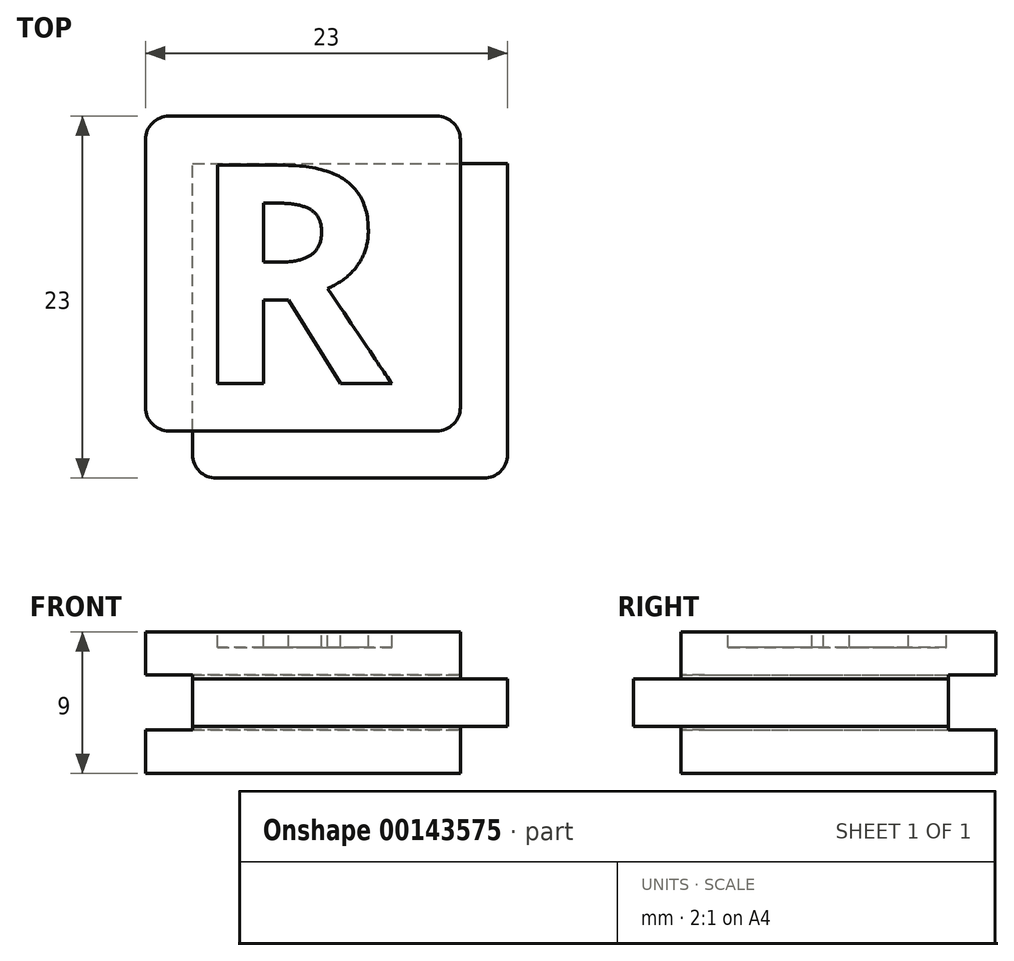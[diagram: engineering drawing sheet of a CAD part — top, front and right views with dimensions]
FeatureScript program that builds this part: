
annotation { "Feature Type Name" : "Feature", "Feature Type Description" : "" }
export const myFeature = defineFeature(function(context is Context, id is Id, definition is map)
    precondition{}
    {
        {
            var Q0;
            Q0=qCreatedBy(makeId("Front.planeOp"),FACE);
            var sketch = newSketch(context, id + "F0", { "sketchPlane" : qUnion([Q0])});
            skLineSegment(sketch, "E0.bottom", {"start": v(10, 4.5) * mm, "end": v(-10, 4.5) * mm});
            skLineSegment(sketch, "E0.top", {"start": v(10, -4.5) * mm, "end": v(-10, -4.5) * mm});
            skLineSegment(sketch, "E0.left", {"start": v(10, 4.5) * mm, "end": v(10, -4.5) * mm});
            skLineSegment(sketch, "E0.right", {"start": v(-10, 4.5) * mm, "end": v(-10, -4.5) * mm});
            skPoint(sketch, "E0.middle", {"position": v(0, 0) * mm});
            skLineSegment(sketch, "E1.bottom", {"start": v(13, 1.5) * mm, "end": v(7, 1.5) * mm});
            skLineSegment(sketch, "E1.top", {"start": v(13, -1.5) * mm, "end": v(7, -1.5) * mm});
            skLineSegment(sketch, "E1.left", {"start": v(13, 1.5) * mm, "end": v(13, -1.5) * mm});
            skLineSegment(sketch, "E1.right", {"start": v(7, 1.5) * mm, "end": v(7, -1.5) * mm});
            skPoint(sketch, "E1.middle", {"position": v(10, 0) * mm});
            skLineSegment(sketch, "E2.bottom", {"start": v(7, 1.5) * mm, "end": v(-7, 1.5) * mm});
            skLineSegment(sketch, "E2.top", {"start": v(7, -1.5) * mm, "end": v(-7, -1.5) * mm});
            skLineSegment(sketch, "E2.right", {"start": v(-7, 1.5) * mm, "end": v(-7, -1.5) * mm});
            skLineSegment(sketch, "E3.bottom", {"start": v(-7, -1.5) * mm, "end": v(-10, -1.5) * mm});
            skLineSegment(sketch, "E3.top", {"start": v(-7, 1.5) * mm, "end": v(-10, 1.5) * mm});
            skLineSegment(sketch, "E3.left", {"start": v(-7, -1.5) * mm, "end": v(-7, 1.5) * mm});
            skLineSegment(sketch, "E3.right", {"start": v(-10, -1.5) * mm, "end": v(-10, 1.5) * mm});
            skSolve(sketch);
        }
        {
            var Q0;
            {var subQ5=sQuery(id+"F0.wireOp",EDGE,"E0.bottom");Q0=makeQuery(id+"F0.imprint","IMPRINT",FACE,{"disambiguationData":[TD([[makeQuery(id+"F0.imprint","IMPRINT",EDGE,{"derivedFrom":subQ5}),1.0]])]});}
            var Q1;
            Q1=makeQuery(id+"F0.imprint","IMPRINT",FACE,{"disambiguationData":[TD([[makeQuery(id+"F0.imprint","IMPRINT",EDGE,{"derivedFrom":sQuery(id+"F0.wireOp",EDGE,"E2.bottom")}),1.0]])]});
            var Q2;
            {var subQ5=sQuery(id+"F0.wireOp",EDGE,"E1.left");Q2=makeQuery(id+"F0.imprint","IMPRINT",FACE,{"disambiguationData":[TD([[makeQuery(id+"F0.imprint","IMPRINT",EDGE,{"derivedFrom":subQ5}),-1.0]])]});}
            var Q3;
            {var subQ5=sQuery(id+"F0.wireOp",EDGE,"E1.right");Q3=makeQuery(id+"F0.imprint","IMPRINT",FACE,{"disambiguationData":[TD([[makeQuery(id+"F0.imprint","IMPRINT",EDGE,{"derivedFrom":subQ5}),1.0]])]});}
            var Q4;
            Q4=makeQuery(id+"F0.imprint","IMPRINT",FACE,{"disambiguationData":[TD([[makeQuery(id+"F0.imprint","IMPRINT",EDGE,{"derivedFrom":sQuery(id+"F0.wireOp",EDGE,"E3.bottom")}),-1.0]])]});
            var Q5;
            {var subQ5=sQuery(id+"F0.wireOp",EDGE,"E0.top");Q5=makeQuery(id+"F0.imprint","IMPRINT",FACE,{"disambiguationData":[TD([[makeQuery(id+"F0.imprint","IMPRINT",EDGE,{"derivedFrom":subQ5}),-1.0]])]});}
            extrude(context, id + "F1", {"entities" : qUnion([Q0, Q1, Q2, Q3, Q4, Q5]), "oppositeDirection" : true, "depth" : 20 * mm});
        }
        {
            var Q0;
            Q0=makeQuery(id+"F0.imprint","IMPRINT",FACE,{"disambiguationData":[TD([[makeQuery(id+"F0.imprint","IMPRINT",EDGE,{"derivedFrom":sQuery(id+"F0.wireOp",EDGE,"E3.bottom")}),-1.0]])]});
            var Q1;
            Q1=makeQuery(id+"F0.imprint","IMPRINT",FACE,{"disambiguationData":[TD([[makeQuery(id+"F0.imprint","IMPRINT",EDGE,{"derivedFrom":sQuery(id+"F0.wireOp",EDGE,"E2.bottom")}),1.0]])]});
            var Q2;
            {var subQ5=sQuery(id+"F0.wireOp",EDGE,"E1.right");Q2=makeQuery(id+"F0.imprint","IMPRINT",FACE,{"disambiguationData":[TD([[makeQuery(id+"F0.imprint","IMPRINT",EDGE,{"derivedFrom":subQ5}),1.0]])]});}
            var Q3;
            {var subQ5=sQuery(id+"F0.wireOp",EDGE,"E1.left");Q3=makeQuery(id+"F0.imprint","IMPRINT",FACE,{"disambiguationData":[TD([[makeQuery(id+"F0.imprint","IMPRINT",EDGE,{"derivedFrom":subQ5}),-1.0]])]});}
            extrude(context, id + "F2", {"entities" : qUnion([Q0, Q1, Q2, Q3]), "operationType" : NewBodyOperationType.ADD, "depth" : 3 * mm});
        }
        {
            var Q0;
            {var subQ0=sQuery(id+"F0.wireOp",EDGE,"E1.left");Q0=makeQuery(id+"F2.boolean.opBoolean","MERGE",FACE,{"derivedFrom":[makeQuery(id+"F1.opExtrude","SWEPT_FACE",FACE,{"disambiguationData":[OSD([subQ0])]}),makeQuery(id+"F2.opExtrude","SWEPT_FACE",FACE,{"disambiguationData":[OSD([subQ0])]})]});}
            var sketch = newSketch(context, id + "F3", { "sketchPlane" : qUnion([Q0])});
            skLineSegment(sketch, "E4.bottom", {"start": v(23, 1.75) * mm, "end": v(17, 1.75) * mm});
            skLineSegment(sketch, "E4.top", {"start": v(23, -1.75) * mm, "end": v(17, -1.75) * mm});
            skLineSegment(sketch, "E4.left", {"start": v(23, 1.75) * mm, "end": v(23, -1.75) * mm});
            skLineSegment(sketch, "E4.right", {"start": v(17, 1.75) * mm, "end": v(17, -1.75) * mm});
            skPoint(sketch, "E4.middle", {"position": v(20, 0) * mm});
            skSolve(sketch);
        }
        {
            var Q0;
            {var subQ1=sQuery(id+"F3.wireOp",EDGE,"E4.bottom");Q0=makeQuery(id+"F3.imprint","IMPRINT",FACE,{"disambiguationData":[TD([[makeQuery(id+"F3.imprint","IMPRINT",EDGE,{"derivedFrom":subQ1}),1.0]])]});}
            var Q1;
            {var subQ1=sQuery(id+"F0.wireOp",EDGE,"E1.left");var subQ8=makeQuery(id+"F1.opExtrude","CAP_EDGE",EDGE,{"disambiguationData":[OSD([subQ1])],"isStart":false});Q1=makeQuery(id+"F3.imprint","IMPRINT",FACE,{"disambiguationData":[TD([[makeQuery(id+"F3.imprint","IMPRINT",EDGE,{"derivedFrom":subQ8}),-1.0]])]});}
            extrude(context, id + "F4", {"entities" : qUnion([Q0, Q1]), "operationType" : NewBodyOperationType.REMOVE, "oppositeDirection" : true, "depth" : 100 * mm});
        }
        {
            var Q0;
            Q0=makeQuery(id+"F4.boolean.opBoolean","COPY",FACE,{"derivedFrom":makeQuery(id+"F4.opExtrude","SWEPT_FACE",FACE,{"disambiguationData":[OSD([sQuery(id+"F3.wireOp",EDGE,"E4.right")])]})});
            var sketch = newSketch(context, id + "F5", { "sketchPlane" : qUnion([Q0])});
            skLineSegment(sketch, "E5.bottom", {"start": v(13, 1.75) * mm, "end": v(7, 1.75) * mm});
            skLineSegment(sketch, "E5.top", {"start": v(13, -1.75) * mm, "end": v(7, -1.75) * mm});
            skLineSegment(sketch, "E5.left", {"start": v(13, 1.75) * mm, "end": v(13, -1.75) * mm});
            skLineSegment(sketch, "E5.right", {"start": v(7, 1.75) * mm, "end": v(7, -1.75) * mm});
            skPoint(sketch, "E5.middle", {"position": v(10, 0) * mm});
            skSolve(sketch);
        }
        {
            var Q0;
            {var subQ3=sQuery(id+"F5.wireOp",EDGE,"E5.left");Q0=makeQuery(id+"F5.imprint","IMPRINT",FACE,{"disambiguationData":[TD([[makeQuery(id+"F5.imprint","IMPRINT",EDGE,{"derivedFrom":subQ3}),-1.0]])]});}
            var Q1;
            {var subQ4=sQuery(id+"F5.wireOp",EDGE,"E5.right");Q1=makeQuery(id+"F5.imprint","IMPRINT",FACE,{"disambiguationData":[TD([[makeQuery(id+"F5.imprint","IMPRINT",EDGE,{"derivedFrom":subQ4}),1.0]])]});}
            extrude(context, id + "F6", {"entities" : qUnion([Q0, Q1]), "operationType" : NewBodyOperationType.REMOVE, "oppositeDirection" : true, "depth" : 100 * mm});
        }
        {
            var Q0;
            Q0=makeQuery(id+"F6.boolean.opBoolean","INTERSECT",EDGE,{"derivedFrom":[makeQuery(id+"F2.opExtrude","CAP_FACE",FACE,{"disambiguationData":[OSD([sQuery(id+"F0.wireOp",EDGE,"E1.bottom"),sQuery(id+"F0.wireOp",EDGE,"E1.top"),sQuery(id+"F0.wireOp",EDGE,"E1.left"),sQuery(id+"F0.wireOp",EDGE,"E2.bottom"),sQuery(id+"F0.wireOp",EDGE,"E2.top"),sQuery(id+"F0.wireOp",EDGE,"E3.bottom"),sQuery(id+"F0.wireOp",EDGE,"E3.top"),sQuery(id+"F0.wireOp",EDGE,"E3.right")])],"isStart":false}),makeQuery(id+"F6.opExtrude","SWEPT_FACE",FACE,{"disambiguationData":[OSD([sQuery(id+"F5.wireOp",EDGE,"E5.right")])]})]});
            var Q1;
            Q1=makeQuery(id+"F2.opExtrude","CAP_EDGE",EDGE,{"disambiguationData":[OSD([sQuery(id+"F0.wireOp",EDGE,"E1.left")])],"isStart":false});
            var Q2;
            {var subQ0=sQuery(id+"F0.wireOp",EDGE,"E0.left");Q2=makeQuery(id+"F1.opExtrude","CAP_EDGE",EDGE,{"disambiguationData":[OSD([subQ0]),TDD([makeQuery(id+"F0.imprint","IMPRINT",EDGE,{"disambiguationData":[TD([[makeQuery(id+"F0.imprint","INTERSECT",VERTEX,{"derivedFrom":[sQuery(id+"F0.wireOp",EDGE,"E0.bottom"),subQ0]}),-1.0]])],"derivedFrom":subQ0})])],"isStart":true});}
            var Q3;
            {var subQ0=sQuery(id+"F0.wireOp",EDGE,"E0.left");Q3=makeQuery(id+"F1.opExtrude","CAP_EDGE",EDGE,{"disambiguationData":[OSD([subQ0]),TDD([makeQuery(id+"F0.imprint","IMPRINT",EDGE,{"disambiguationData":[TD([[makeQuery(id+"F0.imprint","INTERSECT",VERTEX,{"derivedFrom":[sQuery(id+"F0.wireOp",EDGE,"E0.top"),subQ0]}),1.0]])],"derivedFrom":subQ0})])],"isStart":true});}
            var Q4;
            {var subQ0=sQuery(id+"F0.wireOp",EDGE,"E3.right");var subQ1=sQuery(id+"F0.wireOp",EDGE,"E0.right");var subQ3=sQuery(id+"F0.wireOp",EDGE,"E0.top");Q4=makeQuery(id+"F2.boolean.opBoolean","SPLIT",EDGE,{"disambiguationData":[TD([makeQuery(id+"F1.opExtrude","SWEPT_FACE",FACE,{"disambiguationData":[OSD([subQ3])]})])],"derivedFrom":makeQuery(id+"F1.opExtrude","CAP_EDGE",EDGE,{"disambiguationData":[OSD([subQ1,subQ0])],"isStart":true})});}
            var Q5;
            {var subQ1=sQuery(id+"F0.wireOp",EDGE,"E3.right");var subQ2=sQuery(id+"F0.wireOp",EDGE,"E0.right");var subQ3=sQuery(id+"F0.wireOp",EDGE,"E0.bottom");Q5=makeQuery(id+"F2.boolean.opBoolean","SPLIT",EDGE,{"disambiguationData":[TD([makeQuery(id+"F1.opExtrude","SWEPT_FACE",FACE,{"disambiguationData":[OSD([subQ3])]})])],"derivedFrom":makeQuery(id+"F1.opExtrude","CAP_EDGE",EDGE,{"disambiguationData":[OSD([subQ2,subQ1])],"isStart":true})});}
            var Q6;
            Q6=makeQuery(id+"F6.boolean.opBoolean","COPY",EDGE,{"derivedFrom":makeQuery(id+"F6.opExtrude","CAP_EDGE",EDGE,{"disambiguationData":[OSD([sQuery(id+"F5.wireOp",EDGE,"E5.right")])],"isStart":true})});
            var Q7;
            {var subQ0=sQuery(id+"F0.wireOp",EDGE,"E3.right");var subQ1=sQuery(id+"F0.wireOp",EDGE,"E0.right");var subQ2=sQuery(id+"F0.wireOp",EDGE,"E0.bottom");Q7=makeQuery(id+"F4.boolean.opBoolean","SPLIT",EDGE,{"disambiguationData":[TD([makeQuery(id+"F1.opExtrude","SWEPT_FACE",FACE,{"disambiguationData":[OSD([subQ2])]})])],"derivedFrom":makeQuery(id+"F1.opExtrude","CAP_EDGE",EDGE,{"disambiguationData":[OSD([subQ1,subQ0])],"isStart":false})});}
            var Q8;
            {var subQ0=sQuery(id+"F0.wireOp",EDGE,"E3.right");var subQ1=sQuery(id+"F0.wireOp",EDGE,"E0.right");var subQ2=sQuery(id+"F0.wireOp",EDGE,"E0.top");Q8=makeQuery(id+"F4.boolean.opBoolean","SPLIT",EDGE,{"disambiguationData":[TD([makeQuery(id+"F1.opExtrude","SWEPT_FACE",FACE,{"disambiguationData":[OSD([subQ2])]})])],"derivedFrom":makeQuery(id+"F1.opExtrude","CAP_EDGE",EDGE,{"disambiguationData":[OSD([subQ1,subQ0])],"isStart":false})});}
            var Q9;
            Q9=makeQuery(id+"F4.boolean.opBoolean","COPY",EDGE,{"derivedFrom":makeQuery(id+"F4.opExtrude","CAP_EDGE",EDGE,{"disambiguationData":[OSD([sQuery(id+"F3.wireOp",EDGE,"E4.right")])],"isStart":true})});
            var Q10;
            {var subQ0=sQuery(id+"F0.wireOp",EDGE,"E0.left");Q10=makeQuery(id+"F1.opExtrude","CAP_EDGE",EDGE,{"disambiguationData":[OSD([subQ0]),TDD([makeQuery(id+"F0.imprint","IMPRINT",EDGE,{"disambiguationData":[TD([[makeQuery(id+"F0.imprint","INTERSECT",VERTEX,{"derivedFrom":[sQuery(id+"F0.wireOp",EDGE,"E0.bottom"),subQ0]}),-1.0]])],"derivedFrom":subQ0})])],"isStart":false});}
            var Q11;
            {var subQ0=sQuery(id+"F0.wireOp",EDGE,"E0.left");Q11=makeQuery(id+"F1.opExtrude","CAP_EDGE",EDGE,{"disambiguationData":[OSD([subQ0]),TDD([makeQuery(id+"F0.imprint","IMPRINT",EDGE,{"disambiguationData":[TD([[makeQuery(id+"F0.imprint","INTERSECT",VERTEX,{"derivedFrom":[sQuery(id+"F0.wireOp",EDGE,"E0.top"),subQ0]}),1.0]])],"derivedFrom":subQ0})])],"isStart":false});}
            fillet(context, id + "F7", {"entities" : qUnion([Q0, Q1, Q2, Q3, Q4, Q5, Q6, Q7, Q8, Q9, Q10, Q11]), "radius" : 1.5 * mm, "tangentPropagation" : true, "allowEdgeOverflow" : false});
        }
        {
            var Q0;
            Q0=makeQuery(id+"F1.opExtrude","SWEPT_FACE",FACE,{"disambiguationData":[OSD([sQuery(id+"F0.wireOp",EDGE,"E0.bottom")])]});
            var sketch = newSketch(context, id + "F8", { "sketchPlane" : qUnion([Q0])});
            skText(sketch, "E6", { "text": "R", "fontName": "OpenSans-Bold.ttf"});
            skLineSegment(sketch, "E7.0", {"start": v(10.8, 3) * mm, "end": v(-11.07, 3) * mm});
            const initialGuessF8  = {"E6": [-0.00718, 0.003, 1, 0, 0.014]};
            skSetInitialGuess(sketch, initialGuessF8);
            skSolve(sketch);
        }
        {
            var Q0;
            Q0=makeQuery(id+"F8.imprint","IMPRINT",FACE,{"disambiguationData":[TD([[makeQuery(id+"F8.imprint","IMPRINT",EDGE,{"derivedFrom":sQuery(id+"F8.wireOp",EDGE,"E6.sketch_text.stroke-0")}),-1.0]])]});
            extrude(context, id + "F9", {"entities" : qUnion([Q0]), "operationType" : NewBodyOperationType.REMOVE, "oppositeDirection" : true, "depth" : 1 * mm});
        }
    });
